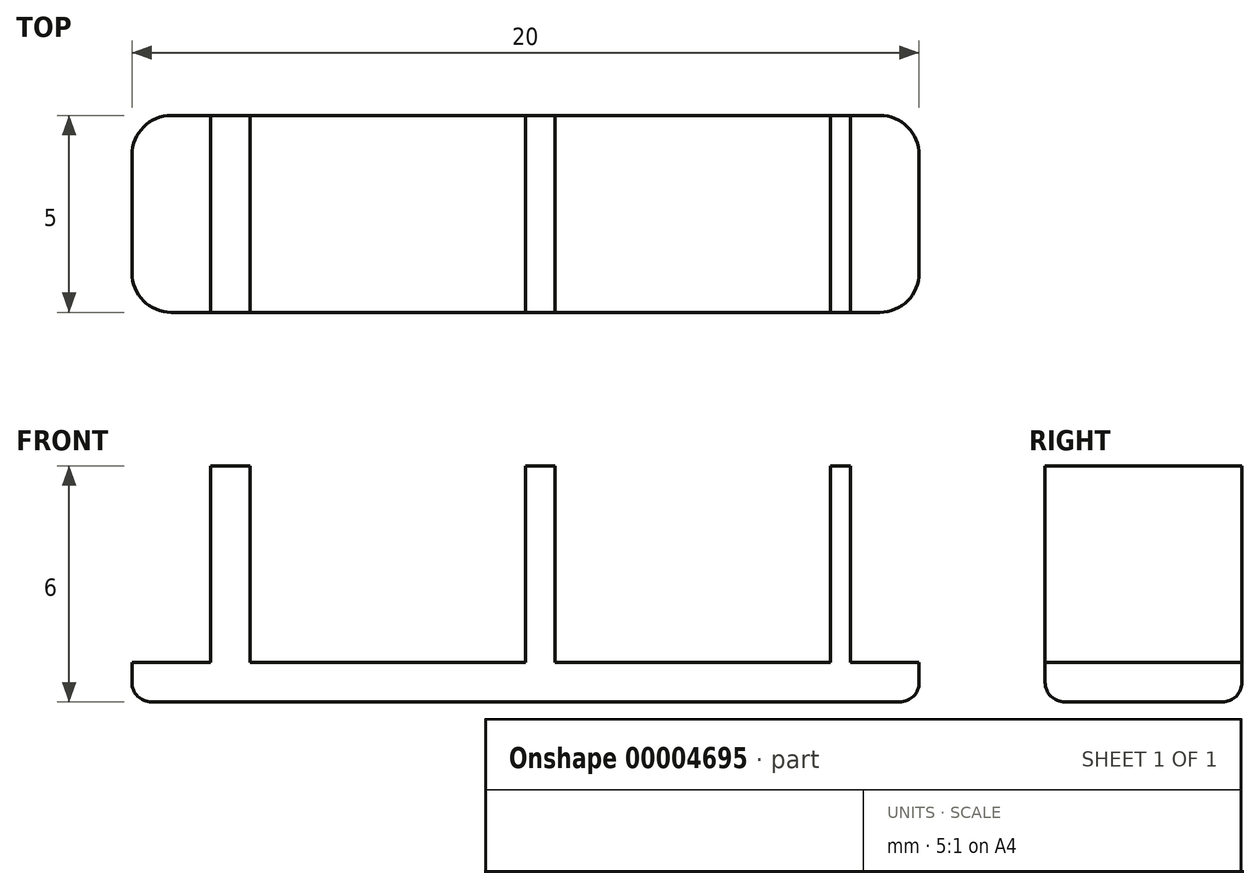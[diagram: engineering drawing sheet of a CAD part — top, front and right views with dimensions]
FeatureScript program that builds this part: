
annotation { "Feature Type Name" : "Feature", "Feature Type Description" : "" }
export const myFeature = defineFeature(function(context is Context, id is Id, definition is map)
    precondition{}
    {
        {
            var Q0;
            Q0=qCreatedBy(makeId("Top.planeOp"),FACE);
            var sketch = newSketch(context, id + "F0", { "sketchPlane" : qUnion([Q0])});
            skLineSegment(sketch, "E0.bottom", {"start": v(0, 0) * mm, "end": v(-20, 0) * mm});
            skLineSegment(sketch, "E0.top", {"start": v(0, 5) * mm, "end": v(-20, 5) * mm});
            skLineSegment(sketch, "E0.left", {"start": v(0, 0) * mm, "end": v(0, 5) * mm});
            skLineSegment(sketch, "E0.right", {"start": v(-20, 0) * mm, "end": v(-20, 5) * mm});
            skSolve(sketch);
        }
        {
            var Q0;
            Q0 = qSketchRegion(id + "F0", true);
            extrude(context, id + "F1", {"entities" : qUnion([Q0]), "depth" : 1 * mm});
        }
        {
            var Q0;
            Q0=makeQuery(id+"F1.opExtrude","CAP_FACE",FACE,{"disambiguationData":[OSD([sQuery(id+"F0.wireOp",EDGE,"E0.bottom"),sQuery(id+"F0.wireOp",EDGE,"E0.top"),sQuery(id+"F0.wireOp",EDGE,"E0.left"),sQuery(id+"F0.wireOp",EDGE,"E0.right")])],"isStart":false});
            var sketch = newSketch(context, id + "F2", { "sketchPlane" : qUnion([Q0])});
            skLineSegment(sketch, "E1.bottom", {"start": v(-18, 5) * mm, "end": v(-17, 5) * mm});
            skLineSegment(sketch, "E1.top", {"start": v(-18, 0) * mm, "end": v(-17, 0) * mm});
            skLineSegment(sketch, "E1.left", {"start": v(-18, 5) * mm, "end": v(-18, 0) * mm});
            skLineSegment(sketch, "E1.right", {"start": v(-17, 5) * mm, "end": v(-17, 0) * mm});
            skLineSegment(sketch, "E2.bottom", {"start": v(-10, 5) * mm, "end": v(-9.25, 5) * mm});
            skLineSegment(sketch, "E2.top", {"start": v(-10, 0) * mm, "end": v(-9.25, 0) * mm});
            skLineSegment(sketch, "E2.left", {"start": v(-10, 5) * mm, "end": v(-10, 0) * mm});
            skLineSegment(sketch, "E2.right", {"start": v(-9.25, 5) * mm, "end": v(-9.25, 0) * mm});
            skLineSegment(sketch, "E3.bottom", {"start": v(-2.25, 5) * mm, "end": v(-1.75, 5) * mm});
            skLineSegment(sketch, "E3.top", {"start": v(-2.25, 0) * mm, "end": v(-1.75, 0) * mm});
            skLineSegment(sketch, "E3.left", {"start": v(-2.25, 5) * mm, "end": v(-2.25, 0) * mm});
            skLineSegment(sketch, "E3.right", {"start": v(-1.75, 5) * mm, "end": v(-1.75, 0) * mm});
            skLineSegment(sketch, "E4", {"start": v(-17, 2.5) * mm, "end": v(-10, 2.5) * mm, "construction": true});
            skLineSegment(sketch, "E5", {"start": v(-9.25, 2.5) * mm, "end": v(-2.25, 2.5) * mm, "construction": true});
            skSolve(sketch);
        }
        {
            var Q0;
            Q0 = qSketchRegion(id + "F2", true);
            extrude(context, id + "F3", {"entities" : qUnion([Q0]), "operationType" : NewBodyOperationType.ADD, "depth" : 5 * mm});
        }
        {
            var Q0;
            Q0=makeQuery(id+"F1.opExtrude","SWEPT_EDGE",EDGE,{"disambiguationData":[OSD([sQuery(id+"F0.wireOp",EDGE,"E0.bottom"),sQuery(id+"F0.wireOp",EDGE,"E0.right")])]});
            var Q1;
            Q1=makeQuery(id+"F1.opExtrude","SWEPT_EDGE",EDGE,{"disambiguationData":[OSD([sQuery(id+"F0.wireOp",EDGE,"E0.top"),sQuery(id+"F0.wireOp",EDGE,"E0.right")])]});
            var Q2;
            Q2=makeQuery(id+"F1.opExtrude","SWEPT_EDGE",EDGE,{"disambiguationData":[OSD([sQuery(id+"F0.wireOp",EDGE,"E0.bottom"),sQuery(id+"F0.wireOp",EDGE,"E0.left")])]});
            var Q3;
            Q3=makeQuery(id+"F1.opExtrude","SWEPT_EDGE",EDGE,{"disambiguationData":[OSD([sQuery(id+"F0.wireOp",EDGE,"E0.top"),sQuery(id+"F0.wireOp",EDGE,"E0.left")])]});
            fillet(context, id + "F4", {"entities" : qUnion([Q0, Q1, Q2, Q3]), "radius" : 1 * mm, "tangentPropagation" : true, "allowEdgeOverflow" : false});
        }
        {
            var Q0;
            Q0=makeQuery(id+"F1.opExtrude","CAP_EDGE",EDGE,{"disambiguationData":[OSD([sQuery(id+"F0.wireOp",EDGE,"E0.bottom")])],"isStart":true});
            var Q1;
            {var subQ0=sQuery(id+"F0.wireOp",EDGE,"E0.bottom");var subQ1=sQuery(id+"F0.wireOp",EDGE,"E0.right");Q1=makeQuery(id+"F4.opFillet","BLEND_EDGE",EDGE,{"blendedFrom":[makeQuery(id+"F1.opExtrude","SWEPT_EDGE",EDGE,{"disambiguationData":[OSD([subQ0,subQ1])]}),makeQuery(id+"F1.opExtrude","CAP_FACE",FACE,{"disambiguationData":[OSD([subQ0,sQuery(id+"F0.wireOp",EDGE,"E0.top"),sQuery(id+"F0.wireOp",EDGE,"E0.left"),subQ1])],"isStart":true})],"blendedInto":[makeQuery(id+"F1.opExtrude","CAP_FACE",FACE,{"disambiguationData":[OSD([subQ0,sQuery(id+"F0.wireOp",EDGE,"E0.top"),sQuery(id+"F0.wireOp",EDGE,"E0.left"),subQ1])],"isStart":true})]});}
            var Q2;
            {var subQ0=sQuery(id+"F0.wireOp",EDGE,"E0.bottom");var subQ1=sQuery(id+"F0.wireOp",EDGE,"E0.left");Q2=makeQuery(id+"F4.opFillet","BLEND_EDGE",EDGE,{"blendedFrom":[makeQuery(id+"F1.opExtrude","SWEPT_EDGE",EDGE,{"disambiguationData":[OSD([subQ0,subQ1])]}),makeQuery(id+"F1.opExtrude","CAP_FACE",FACE,{"disambiguationData":[OSD([subQ0,sQuery(id+"F0.wireOp",EDGE,"E0.top"),subQ1,sQuery(id+"F0.wireOp",EDGE,"E0.right")])],"isStart":true})],"blendedInto":[makeQuery(id+"F1.opExtrude","CAP_FACE",FACE,{"disambiguationData":[OSD([subQ0,sQuery(id+"F0.wireOp",EDGE,"E0.top"),subQ1,sQuery(id+"F0.wireOp",EDGE,"E0.right")])],"isStart":true})]});}
            var Q3;
            Q3=makeQuery(id+"F1.opExtrude","CAP_EDGE",EDGE,{"disambiguationData":[OSD([sQuery(id+"F0.wireOp",EDGE,"E0.left")])],"isStart":true});
            var Q4;
            {var subQ0=sQuery(id+"F0.wireOp",EDGE,"E0.top");var subQ1=sQuery(id+"F0.wireOp",EDGE,"E0.left");Q4=makeQuery(id+"F4.opFillet","BLEND_EDGE",EDGE,{"blendedFrom":[makeQuery(id+"F1.opExtrude","SWEPT_EDGE",EDGE,{"disambiguationData":[OSD([subQ0,subQ1])]}),makeQuery(id+"F1.opExtrude","CAP_FACE",FACE,{"disambiguationData":[OSD([sQuery(id+"F0.wireOp",EDGE,"E0.bottom"),subQ0,subQ1,sQuery(id+"F0.wireOp",EDGE,"E0.right")])],"isStart":true})],"blendedInto":[makeQuery(id+"F1.opExtrude","CAP_FACE",FACE,{"disambiguationData":[OSD([sQuery(id+"F0.wireOp",EDGE,"E0.bottom"),subQ0,subQ1,sQuery(id+"F0.wireOp",EDGE,"E0.right")])],"isStart":true})]});}
            var Q5;
            Q5=makeQuery(id+"F1.opExtrude","CAP_EDGE",EDGE,{"disambiguationData":[OSD([sQuery(id+"F0.wireOp",EDGE,"E0.top")])],"isStart":true});
            var Q6;
            {var subQ0=sQuery(id+"F0.wireOp",EDGE,"E0.top");var subQ1=sQuery(id+"F0.wireOp",EDGE,"E0.right");Q6=makeQuery(id+"F4.opFillet","BLEND_EDGE",EDGE,{"blendedFrom":[makeQuery(id+"F1.opExtrude","SWEPT_EDGE",EDGE,{"disambiguationData":[OSD([subQ0,subQ1])]}),makeQuery(id+"F1.opExtrude","CAP_FACE",FACE,{"disambiguationData":[OSD([sQuery(id+"F0.wireOp",EDGE,"E0.bottom"),subQ0,sQuery(id+"F0.wireOp",EDGE,"E0.left"),subQ1])],"isStart":true})],"blendedInto":[makeQuery(id+"F1.opExtrude","CAP_FACE",FACE,{"disambiguationData":[OSD([sQuery(id+"F0.wireOp",EDGE,"E0.bottom"),subQ0,sQuery(id+"F0.wireOp",EDGE,"E0.left"),subQ1])],"isStart":true})]});}
            fillet(context, id + "F5", {"entities" : qUnion([Q0, Q1, Q2, Q3, Q4, Q5, Q6]), "radius" : .5 * mm, "tangentPropagation" : true, "allowEdgeOverflow" : false});
        }
    });
